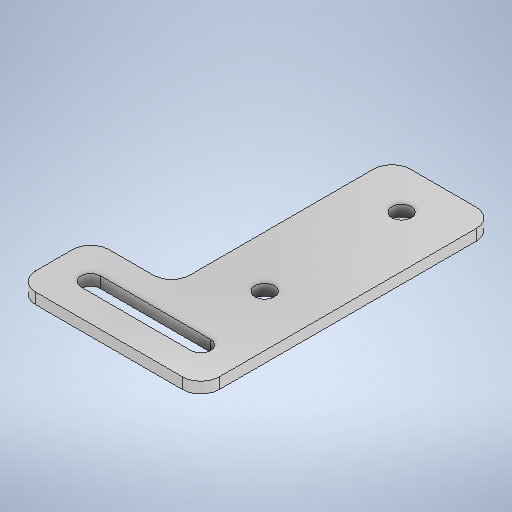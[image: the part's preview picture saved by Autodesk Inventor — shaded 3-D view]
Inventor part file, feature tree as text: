
AUTODESK INVENTOR PART (.ipt)
format: ipt  version: 2025.2 (Build 292293000, 293)  size: 270,336 bytes
history: native  units: mm
features: extrude x2, sketch x2, fillet x1
ambient origin geometry x8: Origin, YZ Plane, XZ Plane, XY Plane, X Axis, Y Axis, Z Axis, Center Point
bodies: Solid1 (feature_tree)
feature tree (5):
  extrude  "Extrusion1"  Depth=80.0mm
  extrude  "Extrusion2"  Depth=5.0mm
  fillet  "Fillet1"  Radius=11.35mm
  sketch  "Sketch1"  dims[d0=50.0mm d1=80.0mm]
  sketch  "Sketch2"  dims[d2=3.0mm d3=0.0mm d4=14.0mm d5=11.35mm d6=37.3mm d7=5.3mm d8=5.3mm d9=10.0mm d10=10.0mm d11=10.0mm d12=5.3mm d13=22.0mm d14=60.0mm d15=0.0mm d16=0.0mm d17=5.0mm]
